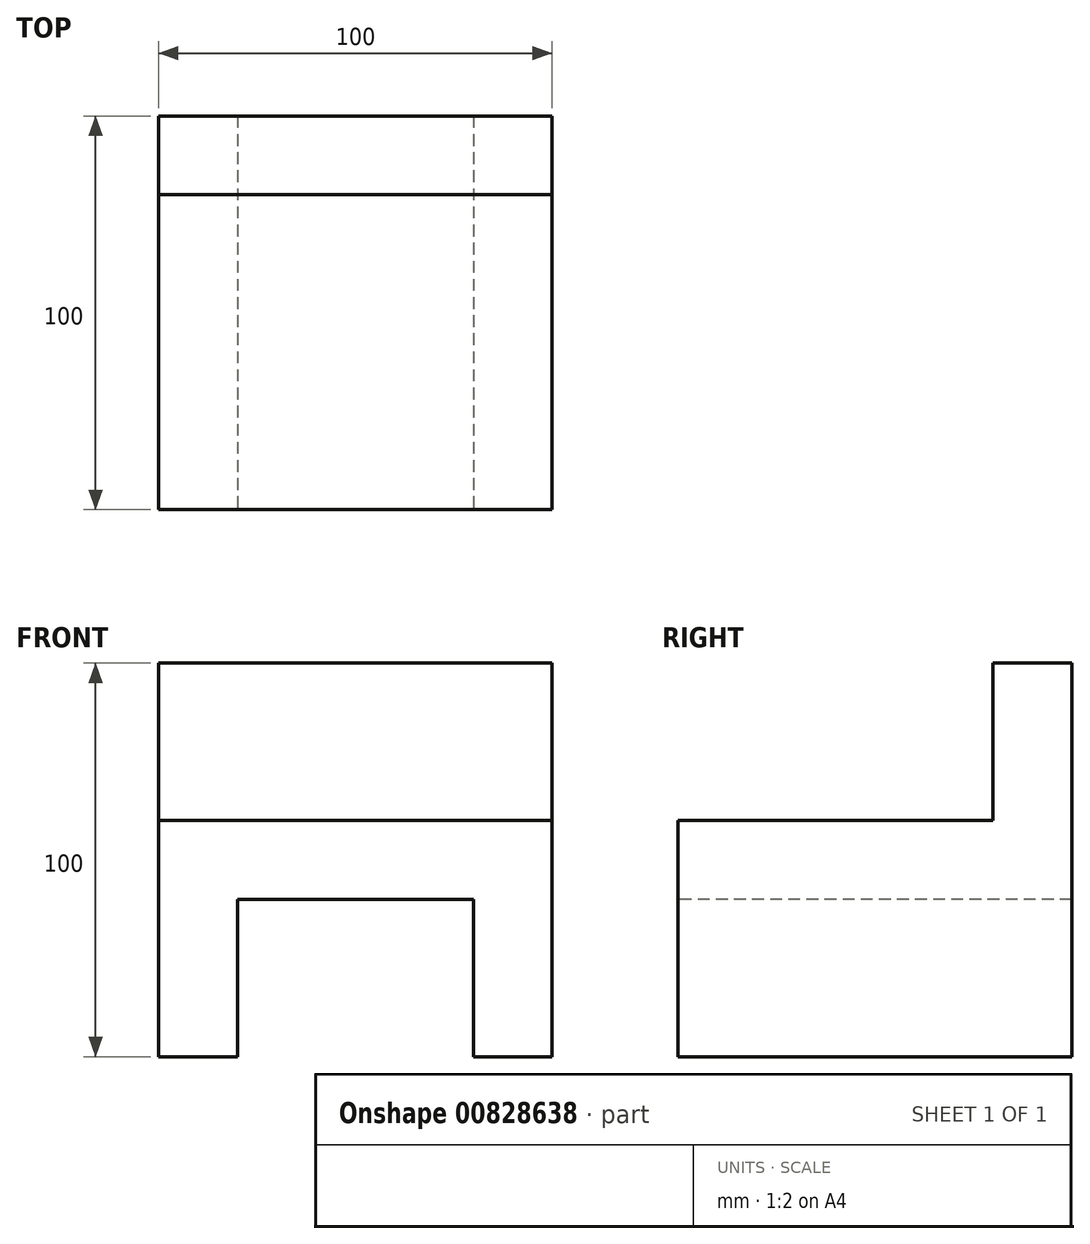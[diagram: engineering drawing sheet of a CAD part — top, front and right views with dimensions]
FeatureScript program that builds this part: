
annotation { "Feature Type Name" : "Feature", "Feature Type Description" : "" }
export const myFeature = defineFeature(function(context is Context, id is Id, definition is map)
    precondition{}
    {
        {
            var Q0;
            Q0=qCreatedBy(makeId("Top.planeOp"),FACE);
            var sketch = newSketch(context, id + "F0", { "sketchPlane" : qUnion([Q0])});
            skLineSegment(sketch, "E0.bottom", {"start": v(50, -50) * mm, "end": v(-50, -50) * mm});
            skLineSegment(sketch, "E0.top", {"start": v(50, 50) * mm, "end": v(-50, 50) * mm});
            skLineSegment(sketch, "E0.left", {"start": v(50, -50) * mm, "end": v(50, 50) * mm});
            skLineSegment(sketch, "E0.right", {"start": v(-50, -50) * mm, "end": v(-50, 50) * mm});
            skPoint(sketch, "E0.middle", {"position": v(0, 0) * mm});
            skSolve(sketch);
        }
        {
            var Q0;
            Q0 = qSketchRegion(id + "F0", true);
            extrude(context, id + "F1", {"entities" : qUnion([Q0]), "depth" : 100 * mm, "offsetDistance" : 25 * mm});
        }
        {
            var Q0;
            Q0=makeQuery(id+"F1.opExtrude","CAP_FACE",FACE,{"disambiguationData":[OSD([sQuery(id+"F0.wireOp",EDGE,"E0.bottom"),sQuery(id+"F0.wireOp",EDGE,"E0.top"),sQuery(id+"F0.wireOp",EDGE,"E0.left"),sQuery(id+"F0.wireOp",EDGE,"E0.right")])],"isStart":false});
            var sketch = newSketch(context, id + "F2", { "sketchPlane" : qUnion([Q0])});
            skLineSegment(sketch, "E1.bottom", {"start": v(-50, -50) * mm, "end": v(50, -50) * mm});
            skLineSegment(sketch, "E1.top", {"start": v(-50, 30) * mm, "end": v(50, 30) * mm});
            skLineSegment(sketch, "E1.left", {"start": v(-50, -50) * mm, "end": v(-50, 30) * mm});
            skLineSegment(sketch, "E1.right", {"start": v(50, -50) * mm, "end": v(50, 30) * mm});
            skSolve(sketch);
        }
        {
            var Q0;
            Q0 = qSketchRegion(id + "F2", true);
            extrude(context, id + "F3", {"entities" : qUnion([Q0]), "operationType" : NewBodyOperationType.REMOVE, "oppositeDirection" : true, "depth" : 40 * mm, "offsetDistance" : 25 * mm});
        }
        {
            var Q0;
            Q0=makeQuery(id+"F1.opExtrude","SWEPT_FACE",FACE,{"disambiguationData":[OSD([sQuery(id+"F0.wireOp",EDGE,"E0.bottom")])]});
            var sketch = newSketch(context, id + "F4", { "sketchPlane" : qUnion([Q0])});
            skLineSegment(sketch, "E2.bottom", {"start": v(-30, 40) * mm, "end": v(30, 40) * mm});
            skLineSegment(sketch, "E2.top", {"start": v(-30, 0) * mm, "end": v(30, 0) * mm});
            skLineSegment(sketch, "E2.left", {"start": v(-30, 40) * mm, "end": v(-30, 0) * mm});
            skLineSegment(sketch, "E2.right", {"start": v(30, 40) * mm, "end": v(30, 0) * mm});
            skSolve(sketch);
        }
        {
            var Q0;
            Q0 = qSketchRegion(id + "F4", true);
            extrude(context, id + "F5", {"entities" : qUnion([Q0]), "operationType" : NewBodyOperationType.REMOVE, "endBound" : BoundingType.THROUGH_ALL, "oppositeDirection" : true, "depth" : 25 * mm, "offsetDistance" : 25 * mm});
        }
    });
